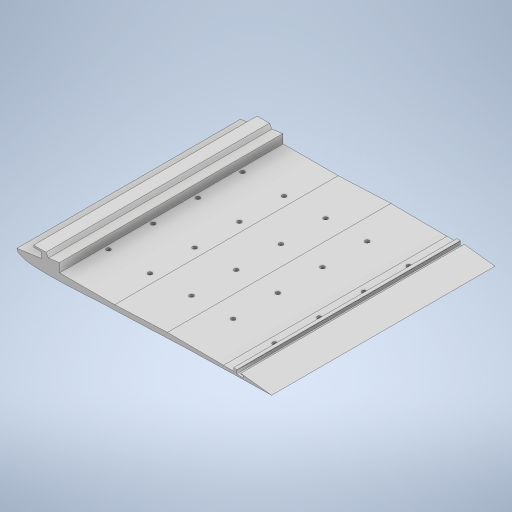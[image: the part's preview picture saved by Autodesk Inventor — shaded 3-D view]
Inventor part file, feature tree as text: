
AUTODESK INVENTOR PART (.ipt)
format: ipt  version: 2024.1 (Build 281209000, 209)  size: 558,592 bytes
history: native  units: in
note: dims shown in document units (in); Inventor stores cm internally (conversion verified against a paired STEP export)
features: sketch x12, extrude x11, other x3, plane x1
ambient origin geometry x8: Origin, YZ Plane, XZ Plane, XY Plane, X Axis, Y Axis, Z Axis, Center Point
bodies: Solid1 (feature_tree)
feature tree (27):
  other  "Airfoil.ipt"
  extrude  "Extrusion1"  Depth=0.1969in
  plane  "Work Plane1"
  extrude  "Extrusion2"  [1 undecoded]
  extrude  "Extrusion3"  Depth=8.4646in TaperAngle=0.0deg
  extrude  "Extrusion4"  Depth=0.1575in
  extrude  "Extrusion5"  Depth=0.1575in
  extrude  "Extrusion6"  Depth=0.1575in
  extrude  "Extrusion7"  Depth=0.1575in
  extrude  "Extrusion8"  Depth=0.1575in
  sketch  "Sketch16"  dims[d32=0.1575in d33=0.1575in]
  extrude  "Extrusion9"  Depth=0.1575in
  extrude  "Extrusion10"  Depth=0.1575in
  extrude  "Extrusion11"  Depth=0.1575in
  other  "Solid1::Airfoil.ipt"
  other  "TaggingFeature1"
  sketch  "Sketch4"  dims[d0=0.3937in d3=0.1969in]
  sketch  "Sketch5"  dims[d4=8.4646in d5=0.0in d6=-8.4646in]
  sketch  "Sketch7"  dims[d7=39.3701in d8=0.0in d10=8.4646in d11=0.0in]
  sketch  "Sketch8"  dims[d21=0.1575in d22=0.1575in]
  sketch  "Sketch10"  dims[d23=0.1575in d24=0.1575in]
  sketch  "Sketch11"  dims[d25=0.1575in d27=0.1575in]
  sketch  "Sketch12"  dims[d28=0.1575in d29=0.1575in]
  sketch  "Sketch13"  dims[d30=0.1575in d31=0.1575in]
  sketch  "Sketch17"  dims[d34=0.1575in d35=0.1575in]
  sketch  "Sketch18"  dims[d36=0.1575in d37=0.1575in]
  sketch  "Sketch19"  dims[d38=0.1575in d39=0.1575in d40=0.1575in d41=0.1575in d42=1.9685in d43=0.0in d44=8.4646in d45=0.0in d46=8.4646in d47=0.0in d48=8.4646in d49=0.0in d50=8.4646in d51=0.0in d52=8.4646in d53=0.0in d54=1.9685in d55=1.1811in d56=0.315in d57=0.0in d59=0.4921in d60=0.0984in d61=0.3937in d63=1.1811in d64=0.4921in d65=0.3937in d66=1.7717in d67=0.0in]
note: 1 required parameter value undecoded (feature->parameter linkage not recoverable at this tier; creation-order binding heuristic only, values carry confidence <= 0.55)
